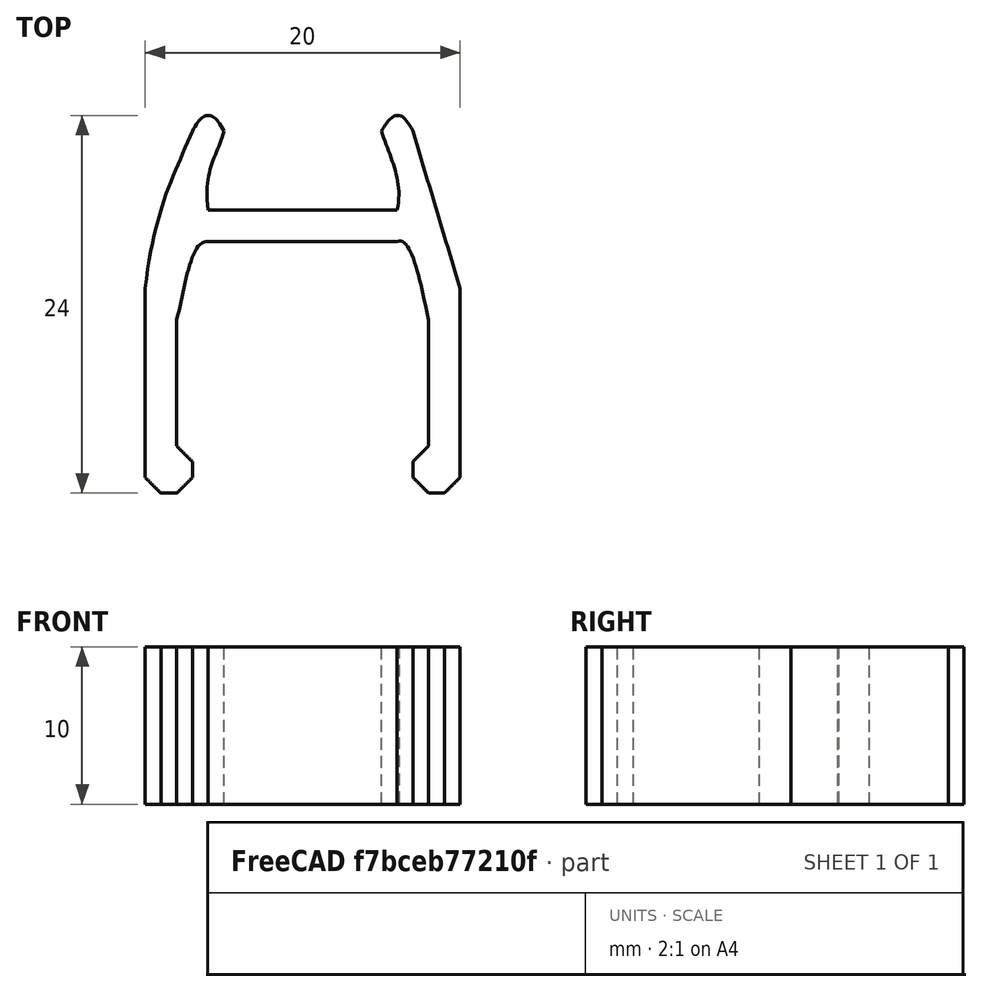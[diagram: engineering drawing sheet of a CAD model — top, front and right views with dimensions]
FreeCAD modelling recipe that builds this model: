
FCSTD DOCUMENT  (FreeCAD 0.19R24276 (Git))
Label: SpeedDriverClip
License: All rights reserved
LicenseURL: http://en.wikipedia.org/wiki/All_rights_reserved
objects: Sketcher::SketchObject×1, Part::Feature×1, PartDesign::FeatureBase×1, PartDesign::Pad×1, PartDesign::Body×1
note: 6 computed .brp shape members not serialized (recipe doc carries the construction recipe); baked Part::Feature solids carry a one-line shape summary decoded from their .brp

FEATURE [Sketcher::SketchObject] Sketch
  FullyConstrained = true
  MapMode = 5
  Support = -> [XY_Plane]
FEATURE [Part::Feature] path2076
  shape: bbox 20 x 24.23 x 2e-07 mm, 0 faces, 0 solids (baked)
FEATURE [PartDesign::FeatureBase] BaseFeature
  BaseFeature = -> path2076
FEATURE [PartDesign::Pad] Pad
  BaseFeature = -> BaseFeature
  Direction = (1,1,1)
  Length = 10
  Length2 = 100
  Profile = -> BaseFeature
  Type = 0
FEATURE [PartDesign::Body] Body
  BaseFeature = -> path2076
  Group = -> [BaseFeature,Sketch,Pad]
  Origin = -> Origin
  Tip = -> Pad
